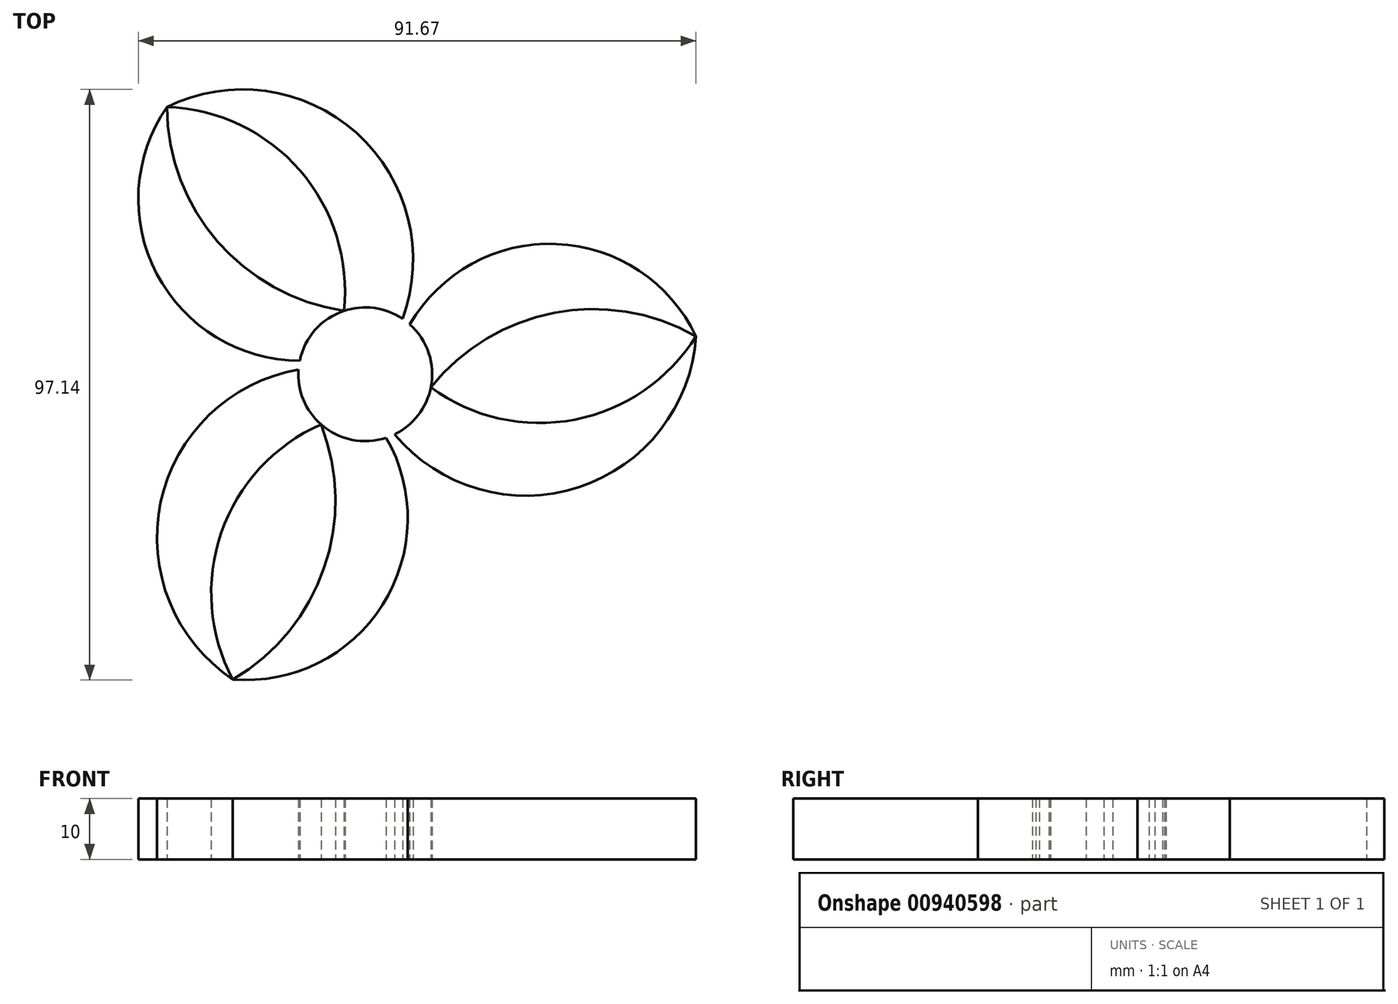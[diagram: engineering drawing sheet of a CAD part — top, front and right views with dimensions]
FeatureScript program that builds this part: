
annotation { "Feature Type Name" : "Feature", "Feature Type Description" : "" }
export const myFeature = defineFeature(function(context is Context, id is Id, definition is map)
    precondition{}
    {
        {
            var Q0;
            Q0=qCreatedBy(makeId("Top.planeOp"),FACE);
            var sketch = newSketch(context, id + "F0", { "sketchPlane" : qUnion([Q0])});
            skCircle(sketch, "E0", {"center": v(0, 0) * mm, "radius": 11 * mm});
            skArc(sketch, "E1", {"start": v(-3.51, 10.42) * mm, "mid": v(-10.75, 33.53) * mm, "end": v(-32.6, 43.95) * mm});
            skArc(sketch, "E2", {"start": v(6.14, 9.13) * mm, "mid": v(-1.43, 39.66) * mm, "end": v(-32.6, 43.95) * mm});
            skArc(sketch, "E3", {"start": v(-32.6, 43.95) * mm, "mid": v(-24.24, 21.82) * mm, "end": v(-3.51, 10.42) * mm});
            skArc(sketch, "E4", {"start": v(-32.6, 43.95) * mm, "mid": v(-34.28, 16.5) * mm, "end": v(-10.77, 2.23) * mm});
            skArc(sketch, "E5.1.0", {"start": v(-21.76, -50.2) * mm, "mid": v(2.85, -37.93) * mm, "end": v(3.45, -10.44) * mm});
            skArc(sketch, "E5.2.0", {"start": v(54.36, 6.26) * mm, "mid": v(31.43, 21.43) * mm, "end": v(7.32, 8.21) * mm});
            skArc(sketch, "E6.1.0", {"start": v(-21.76, -50.2) * mm, "mid": v(-6.77, -31.9) * mm, "end": v(-7.27, -8.25) * mm});
            skArc(sketch, "E6.2.0", {"start": v(54.36, 6.26) * mm, "mid": v(31.01, 10.09) * mm, "end": v(10.78, -2.17) * mm});
            skArc(sketch, "E7.1.0", {"start": v(-7.27, -8.25) * mm, "mid": v(-23.66, -26.07) * mm, "end": v(-21.76, -50.2) * mm});
            skArc(sketch, "E7.2.0", {"start": v(10.78, -2.17) * mm, "mid": v(34.4, -7.46) * mm, "end": v(54.36, 6.26) * mm});
            skArc(sketch, "E8.1.0", {"start": v(-10.97, 0.75) * mm, "mid": v(-33.63, -21.07) * mm, "end": v(-21.76, -50.2) * mm});
            skArc(sketch, "E8.2.0", {"start": v(4.84, -9.88) * mm, "mid": v(35.07, -18.6) * mm, "end": v(54.36, 6.26) * mm});
            skSolve(sketch);
        }
        {
            var Q0;
            {var subQ0=sQuery(id+"F0.wireOp",EDGE,"E3");Q0=makeQuery(id+"F0.imprint","IMPRINT",FACE,{"disambiguationData":[TD([[makeQuery(id+"F0.imprint","IMPRINT",EDGE,{"derivedFrom":subQ0}),-1.0]])]});}
            var Q1;
            {var subQ0=sQuery(id+"F0.wireOp",EDGE,"E1");Q1=makeQuery(id+"F0.imprint","IMPRINT",FACE,{"disambiguationData":[TD([[makeQuery(id+"F0.imprint","IMPRINT",EDGE,{"derivedFrom":subQ0}),-1.0]])]});}
            var Q2;
            {var subQ0=sQuery(id+"F0.wireOp",EDGE,"E5.2.0");Q2=makeQuery(id+"F0.imprint","IMPRINT",FACE,{"disambiguationData":[TD([[makeQuery(id+"F0.imprint","IMPRINT",EDGE,{"derivedFrom":subQ0}),1.0]])]});}
            var Q3;
            {var subQ0=sQuery(id+"F0.wireOp",EDGE,"E7.2.0");Q3=makeQuery(id+"F0.imprint","IMPRINT",FACE,{"disambiguationData":[TD([[makeQuery(id+"F0.imprint","IMPRINT",EDGE,{"derivedFrom":subQ0}),-1.0]])]});}
            var Q4;
            {var subQ0=sQuery(id+"F0.wireOp",EDGE,"E5.1.0");Q4=makeQuery(id+"F0.imprint","IMPRINT",FACE,{"disambiguationData":[TD([[makeQuery(id+"F0.imprint","IMPRINT",EDGE,{"derivedFrom":subQ0}),1.0]])]});}
            var Q5;
            {var subQ0=sQuery(id+"F0.wireOp",EDGE,"E7.1.0");Q5=makeQuery(id+"F0.imprint","IMPRINT",FACE,{"disambiguationData":[TD([[makeQuery(id+"F0.imprint","IMPRINT",EDGE,{"derivedFrom":subQ0}),-1.0]])]});}
            extrude(context, id + "F1", {"entities" : qUnion([Q0, Q1, Q2, Q3, Q4, Q5]), "depth" : 10 * mm, "offsetDistance" : 25.4 * mm});
        }
    });
